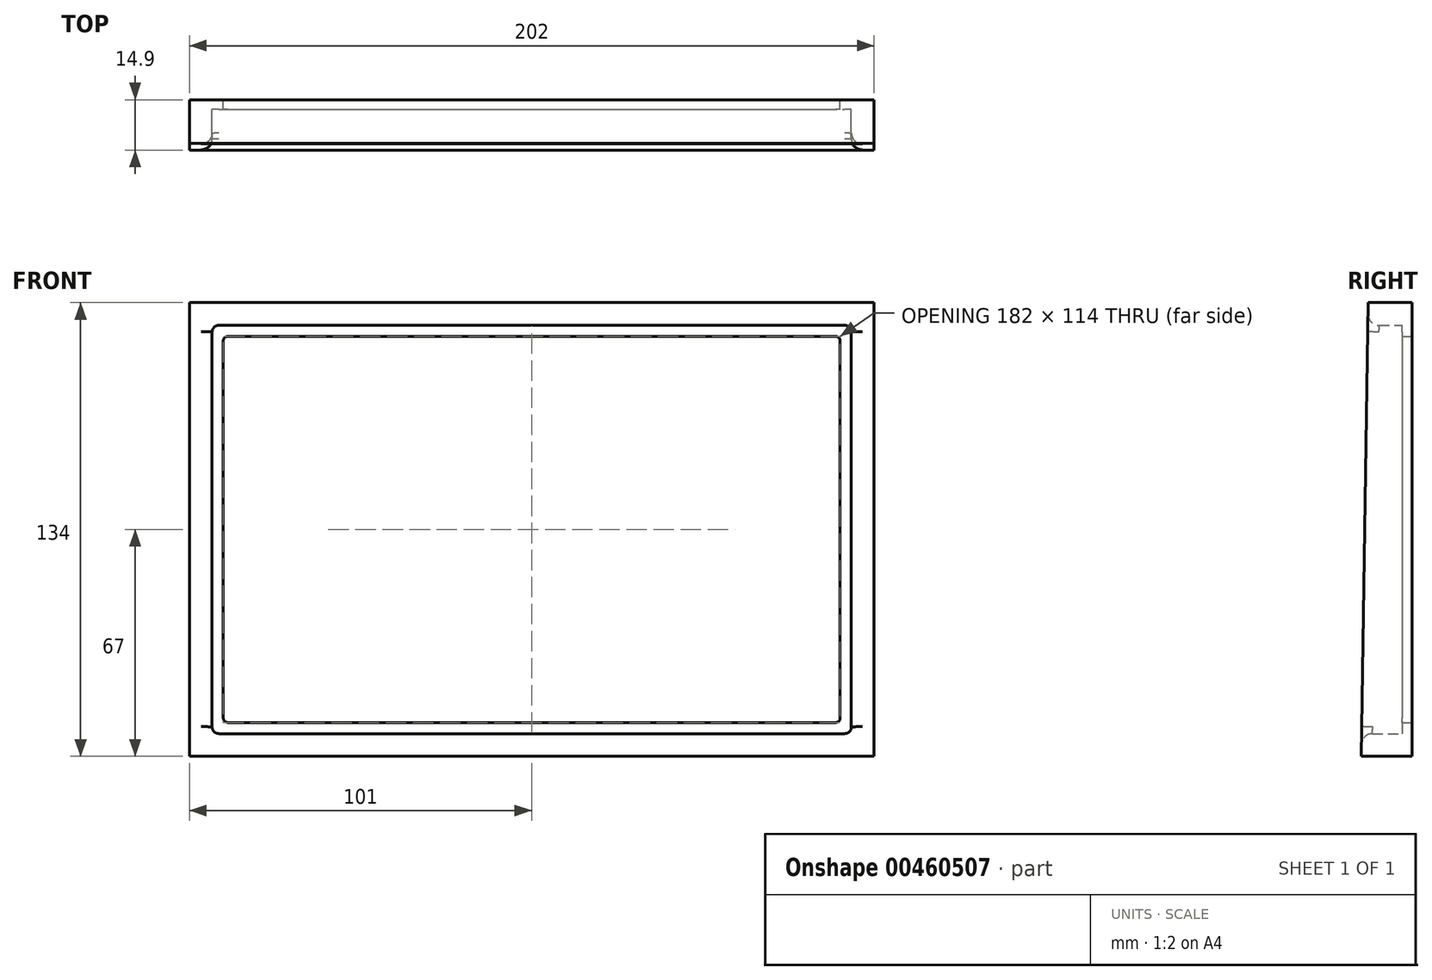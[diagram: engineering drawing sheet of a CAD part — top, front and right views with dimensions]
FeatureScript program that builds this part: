
annotation { "Feature Type Name" : "Feature", "Feature Type Description" : "" }
export const myFeature = defineFeature(function(context is Context, id is Id, definition is map)
    precondition{}
    {
        {
            var Q0;
            Q0=qCreatedBy(makeId("Front.planeOp"),FACE);
            var sketch = newSketch(context, id + "F0", { "sketchPlane" : qUnion([Q0])});
            skLineSegment(sketch, "E0.bottom", {"start": v(-91, 57) * mm, "end": v(91, 57) * mm});
            skLineSegment(sketch, "E0.top", {"start": v(-91, -57) * mm, "end": v(91, -57) * mm});
            skLineSegment(sketch, "E0.left", {"start": v(-91, 57) * mm, "end": v(-91, -57) * mm});
            skLineSegment(sketch, "E0.right", {"start": v(91, 57) * mm, "end": v(91, -57) * mm});
            skLineSegment(sketch, "E1", {"start": v(-91, 0) * mm, "end": v(0, 0) * mm, "construction": true});
            skPoint(sketch, "E1.startSnap0", {"position": v(-91, 0) * mm});
            skLineSegment(sketch, "E2", {"start": v(0, 0) * mm, "end": v(0, 57) * mm, "construction": true});
            skLineSegment(sketch, "E3.0", {"start": v(-101, 67) * mm, "end": v(-101, -67) * mm});
            skLineSegment(sketch, "E3.1", {"start": v(-101, 67) * mm, "end": v(101, 67) * mm});
            skLineSegment(sketch, "E3.2", {"start": v(101, 67) * mm, "end": v(101, -67) * mm});
            skLineSegment(sketch, "E3.3", {"start": v(-101, -67) * mm, "end": v(101, -67) * mm});
            skSolve(sketch);
        }
        {
            var Q0;
            Q0 = qSketchRegion(id + "F0", true);
            extrude(context, id + "F1", {"entities" : qUnion([Q0]), "depth" : 2.9 * mm});
        }
        {
            var Q0;
            Q0=makeQuery(id+"F1.opExtrude","CAP_FACE",FACE,{"disambiguationData":[OSD([sQuery(id+"F0.wireOp",EDGE,"E0.bottom"),sQuery(id+"F0.wireOp",EDGE,"E0.top"),sQuery(id+"F0.wireOp",EDGE,"E0.left"),sQuery(id+"F0.wireOp",EDGE,"E0.right"),sQuery(id+"F0.wireOp",EDGE,"E3.0"),sQuery(id+"F0.wireOp",EDGE,"E3.1"),sQuery(id+"F0.wireOp",EDGE,"E3.2"),sQuery(id+"F0.wireOp",EDGE,"E3.3")])],"isStart":false});
            var sketch = newSketch(context, id + "F2", { "sketchPlane" : qUnion([Q0])});
            skLineSegment(sketch, "E4.0", {"start": v(-94.3, 60.3) * mm, "end": v(94.3, 60.3) * mm});
            skLineSegment(sketch, "E4.1", {"start": v(-94.3, 60.3) * mm, "end": v(-94.3, -60.3) * mm});
            skLineSegment(sketch, "E4.2", {"start": v(-94.3, -60.3) * mm, "end": v(94.3, -60.3) * mm});
            skLineSegment(sketch, "E4.3", {"start": v(94.3, 60.3) * mm, "end": v(94.3, -60.3) * mm});
            skLineSegment(sketch, "E5.0", {"start": v(-101, 67) * mm, "end": v(101, 67) * mm});
            skLineSegment(sketch, "E6.0", {"start": v(-101, 67) * mm, "end": v(-101, -67) * mm});
            skLineSegment(sketch, "E7.0", {"start": v(101, 67) * mm, "end": v(101, -67) * mm});
            skLineSegment(sketch, "E8.0", {"start": v(-101, -67) * mm, "end": v(101, -67) * mm});
            skSolve(sketch);
        }
        {
            var Q0;
            Q0 = qSketchRegion(id + "F2", true);
            extrude(context, id + "F3", {"entities" : qUnion([Q0]), "operationType" : NewBodyOperationType.ADD, "depth" : 12 * mm});
        }
        {
            var Q0;
            Q0=makeQuery(id+"F3.opExtrude","SWEPT_EDGE",EDGE,{"disambiguationData":[OSD([sQuery(id+"F2.wireOp",EDGE,"E4.2"),sQuery(id+"F2.wireOp",EDGE,"E4.3")])]});
            var Q1;
            Q1=makeQuery(id+"F3.opExtrude","SWEPT_EDGE",EDGE,{"disambiguationData":[OSD([sQuery(id+"F2.wireOp",EDGE,"E4.1"),sQuery(id+"F2.wireOp",EDGE,"E4.2")])]});
            var Q2;
            Q2=makeQuery(id+"F3.opExtrude","SWEPT_EDGE",EDGE,{"disambiguationData":[OSD([sQuery(id+"F2.wireOp",EDGE,"E4.0"),sQuery(id+"F2.wireOp",EDGE,"E4.1")])]});
            var Q3;
            Q3=makeQuery(id+"F3.opExtrude","SWEPT_EDGE",EDGE,{"disambiguationData":[OSD([sQuery(id+"F2.wireOp",EDGE,"E4.0"),sQuery(id+"F2.wireOp",EDGE,"E4.3")])]});
            fillet(context, id + "F4", {"entities" : qUnion([Q0, Q1, Q2, Q3]), "radius" : 2 * mm, "tangentPropagation" : true, "allowEdgeOverflow" : false});
        }
        {
            var Q0;
            Q0=makeQuery(id+"F1.opExtrude","SWEPT_EDGE",EDGE,{"disambiguationData":[OSD([sQuery(id+"F0.wireOp",EDGE,"E0.top"),sQuery(id+"F0.wireOp",EDGE,"E0.left")])]});
            var Q1;
            Q1=makeQuery(id+"F1.opExtrude","SWEPT_EDGE",EDGE,{"disambiguationData":[OSD([sQuery(id+"F0.wireOp",EDGE,"E0.top"),sQuery(id+"F0.wireOp",EDGE,"E0.right")])]});
            var Q2;
            Q2=makeQuery(id+"F1.opExtrude","SWEPT_EDGE",EDGE,{"disambiguationData":[OSD([sQuery(id+"F0.wireOp",EDGE,"E0.bottom"),sQuery(id+"F0.wireOp",EDGE,"E0.right")])]});
            var Q3;
            Q3=makeQuery(id+"F1.opExtrude","SWEPT_EDGE",EDGE,{"disambiguationData":[OSD([sQuery(id+"F0.wireOp",EDGE,"E0.bottom"),sQuery(id+"F0.wireOp",EDGE,"E0.left")])]});
            fillet(context, id + "F5", {"entities" : qUnion([Q0, Q1, Q2, Q3]), "radius" : 1.3 * mm, "tangentPropagation" : true, "allowEdgeOverflow" : false});
        }
        {
            var Q0;
            Q0=makeQuery(id+"F3.boolean.opBoolean","MERGE",FACE,{"derivedFrom":[makeQuery(id+"F1.opExtrude","SWEPT_FACE",FACE,{"disambiguationData":[OSD([sQuery(id+"F0.wireOp",EDGE,"E3.0")])]}),makeQuery(id+"F3.opExtrude","SWEPT_FACE",FACE,{"disambiguationData":[OSD([sQuery(id+"F2.wireOp",EDGE,"E6.0")])]})]});
            var sketch = newSketch(context, id + "F6", { "sketchPlane" : qUnion([Q0])});
            skLineSegment(sketch, "E9.0", {"start": v(14.9, 67) * mm, "end": v(14.9, -67) * mm});
            skLineSegment(sketch, "E10.0", {"start": v(14.9, 67) * mm, "end": v(0, 67) * mm});
            skLineSegment(sketch, "E11", {"start": v(14.9, -67) * mm, "end": v(12.9, 67) * mm});
            skSolve(sketch);
        }
        {
            var Q0;
            Q0 = qSketchRegion(id + "F6", true);
            extrude(context, id + "F7", {"entities" : qUnion([Q0]), "operationType" : NewBodyOperationType.REMOVE, "endBound" : BoundingType.THROUGH_ALL, "oppositeDirection" : true, "depth" : 25 * mm});
        }
        {
            var Q0;
            Q0=makeQuery(id+"F7.boolean.opBoolean","INTERSECT",EDGE,{"derivedFrom":[makeQuery(id+"F3.opExtrude","SWEPT_FACE",FACE,{"disambiguationData":[OSD([sQuery(id+"F2.wireOp",EDGE,"E4.0")])]}),makeQuery(id+"F7.opExtrude","SWEPT_FACE",FACE,{"disambiguationData":[OSD([sQuery(id+"F6.wireOp",EDGE,"E11")])]})]});
            fillet(context, id + "F8", {"entities" : qUnion([Q0]), "radius" : 3.2 * mm, "tangentPropagation" : true, "allowEdgeOverflow" : false});
        }
    });
